# Revit family: 303_R421X_
name_source: partatom
category: Pipe Accessories
revit_build: Autodesk Revit 2018 (Build: 20170223_1515(x64)
units: mm (PartAtom-declared; Revit-internal decimal feet)

## family parameters
Always vertical = Yes
Cut with Voids When Loaded = No
Part Type = Valve - Breaks Into
Round Connector Dimension = Use Diameter
Shared = No
Work Plane-Based = No

## types (4) — shared parameters
CAT0 = Yes
CAT1 = No
Description = Micrometric angle valve with thermostatic option
L2D_Min = 3048 mm
M1 = 21 mm  [stored 0.0688976 ft]
M3 = 23 mm  [stored 0.0754593 ft]
M3__ve = -23 mm  [stored -0.0754593 ft]
Manufacturer = Giacomini
QmdConnectorList = 301;D;302;D1
SW2 = No
URL = http://www.giacomini.com
X1 = 23 mm  [stored 0.0754593 ft]
X2 = 21 mm  [stored 0.0688976 ft]
Z1 = 10 mm  [stored 0.0328084 ft]
magiPartTypeId = 303
magiProductFamilyId = R421X*
zero-valued in all types: MC_Default_elevation

## per-type parameters (varying)
- R421X132: B1=7 mm  [stored 0.0229659 ft]; B3=8 mm  [stored 0.0262467 ft]; B4=10 mm  [stored 0.0328084 ft]; CenSd_K1_6=10 mm  [stored 0.0328084 ft]; CenSd_W2_6=12 mm  [stored 0.0393701 ft]; D=10 mm; D1=10 mm; G1=8 mm  [stored 0.0262467 ft]; G3=10 mm  [stored 0.0328084 ft]; H3=4 mm  [stored 0.0131234 ft]; H3__ve=-4 mm  [stored -0.0131234 ft]; HLL=7 mm  [stored 0.0229659 ft]; J=20 mm  [stored 0.0656168 ft]; J3=9 mm  [stored 0.0295276 ft]; J5=30 mm  [stored 0.0984252 ft]; K1=11 mm  [stored 0.0360892 ft]; KH=8 mm  [stored 0.0262467 ft]; KH__ve=-8 mm  [stored -0.0262467 ft]; L=38 mm  [stored 0.124672 ft]; L2=49 mm; L2D=38 mm  [stored 0.124672 ft]; L3=4 mm  [stored 0.0131234 ft]; L4=4 mm  [stored 0.0131234 ft]; L4__ve=-4 mm  [stored -0.0131234 ft]; L5=2 mm  [stored 0.00656168 ft]; R1=8 mm  [stored 0.0262467 ft]; SW1=Yes; SW3=No; SW4=Yes; W1=11 mm  [stored 0.0360892 ft]; W2=14 mm  [stored 0.0459318 ft]; W2D=10 mm  [stored 0.0328084 ft]; W3=9 mm  [stored 0.0295276 ft]; X11=36 mm; X4=5 mm  [stored 0.0164042 ft]; Z2=5 mm  [stored 0.0164042 ft]; Z3=7 mm  [stored 0.0229659 ft]; Z4=12 mm  [stored 0.0393701 ft]
- R421X035: B1=12 mm  [stored 0.0393701 ft]; B3=14 mm  [stored 0.0459318 ft]; B4=17 mm; CenSd_K1_6=17 mm; CenSd_W2_6=20 mm  [stored 0.0656168 ft]; D=25 mm; D1=25 mm; G1=15 mm  [stored 0.0492126 ft]; G3=17 mm; H3=8 mm  [stored 0.0262467 ft]; H3__ve=-8 mm  [stored -0.0262467 ft]; HLL=16 mm  [stored 0.0524934 ft]; J=31 mm; J3=11 mm  [stored 0.0360892 ft]; J5=39 mm; K1=20 mm  [stored 0.0656168 ft]; KH=12 mm  [stored 0.0393701 ft]; KH__ve=-12 mm  [stored -0.0393701 ft]; L=54 mm; L2=70 mm; L2D=54 mm; L3=11 mm  [stored 0.0360892 ft]; L4=11 mm  [stored 0.0360892 ft]; L4__ve=-11 mm  [stored -0.0360892 ft]; L5=5 mm  [stored 0.0164042 ft]; R1=16 mm  [stored 0.0524934 ft]; SW1=No; SW3=Yes; SW4=No; W1=18 mm; W2=23 mm  [stored 0.0754593 ft]; W2D=25 mm  [stored 0.082021 ft]; W3=16 mm  [stored 0.0524934 ft]; X11=49 mm; X4=8 mm  [stored 0.0262467 ft]; Z2=6 mm  [stored 0.019685 ft]; Z3=9 mm  [stored 0.0295276 ft]; Z4=19 mm  [stored 0.062336 ft]
- R421X034: B1=10 mm  [stored 0.0328084 ft]; B3=11 mm  [stored 0.0360892 ft]; B4=14 mm  [stored 0.0459318 ft]; CenSd_K1_6=14 mm  [stored 0.0459318 ft]; CenSd_W2_6=16 mm  [stored 0.0524934 ft]; D=20 mm; D1=20 mm; G1=13 mm; G3=15 mm  [stored 0.0492126 ft]; H3=6 mm  [stored 0.019685 ft]; H3__ve=-6 mm  [stored -0.019685 ft]; HLL=11 mm  [stored 0.0360892 ft]; J=25 mm  [stored 0.082021 ft]; J3=9 mm  [stored 0.0295276 ft]; J5=30 mm  [stored 0.0984252 ft]; K1=16 mm  [stored 0.0524934 ft]; KH=10 mm  [stored 0.0328084 ft]; KH__ve=-10 mm  [stored -0.0328084 ft]; L=45 mm; L2=58 mm; L2D=45 mm; L3=7 mm  [stored 0.0229659 ft]; L4=7 mm  [stored 0.0229659 ft]; L4__ve=-7 mm; L5=4 mm  [stored 0.0131234 ft]; R1=13 mm; SW1=No; SW3=Yes; SW4=No; W1=15 mm  [stored 0.0492126 ft]; W2=19 mm  [stored 0.062336 ft]; W2D=20 mm  [stored 0.0656168 ft]; W3=13 mm; X11=41 mm; X4=7 mm  [stored 0.0229659 ft]; Z2=5 mm  [stored 0.0164042 ft]; Z3=7 mm  [stored 0.0229659 ft]; Z4=15 mm  [stored 0.0492126 ft]
- R421X133: B1=8 mm  [stored 0.0262467 ft]; B3=9 mm  [stored 0.0295276 ft]; B4=12 mm  [stored 0.0393701 ft]; CenSd_K1_6=11 mm  [stored 0.0360892 ft]; CenSd_W2_6=13 mm; D=15 mm; D1=15 mm; G1=10 mm  [stored 0.0328084 ft]; G3=12 mm  [stored 0.0393701 ft]; H3=5 mm  [stored 0.0164042 ft]; H3__ve=-5 mm  [stored -0.0164042 ft]; HLL=8 mm  [stored 0.0262467 ft]; J=23 mm  [stored 0.0754593 ft]; J3=9 mm  [stored 0.0295276 ft]; J5=31 mm; K1=13 mm; KH=9 mm  [stored 0.0295276 ft]; KH__ve=-9 mm; L=40 mm; L2=51 mm; L2D=40 mm; L3=5 mm  [stored 0.0164042 ft]; L4=5 mm  [stored 0.0164042 ft]; L4__ve=-5 mm  [stored -0.0164042 ft]; L5=3 mm  [stored 0.00984252 ft]; R1=11 mm  [stored 0.0360892 ft]; SW1=Yes; SW3=No; SW4=Yes; W1=12 mm  [stored 0.0393701 ft]; W2=15 mm  [stored 0.0492126 ft]; W2D=15 mm  [stored 0.0492126 ft]; W3=11 mm  [stored 0.0360892 ft]; X11=37 mm; X4=6 mm  [stored 0.019685 ft]; Z2=5 mm  [stored 0.0164042 ft]; Z3=7 mm  [stored 0.0229659 ft]; Z4=14 mm  [stored 0.0459318 ft]

note: column(s) folded — value = type name in every type: magiProductCode, magiProductId

note: [stored X ft] marks values corroborated as IEEE doubles in the binary element streams (Revit-internal decimal feet)

## geometry (parser evidence)
native form markers: Sweep x2
no freeform markers — native parametric forms only
